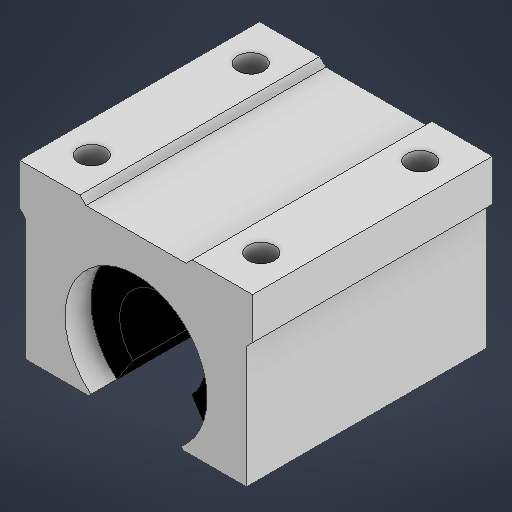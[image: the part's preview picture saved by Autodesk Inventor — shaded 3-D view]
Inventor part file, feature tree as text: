
AUTODESK INVENTOR PART (.ipt)
format: ipt  version: 2025.1 (Build 291241000, 241)  size: 246,272 bytes
history: native  units: mm
features: extrude x3, sketch x2
ambient origin geometry x8: Origin, YZ Plane, XZ Plane, XY Plane, X Axis, Y Axis, Z Axis, Center Point
bodies: Solid1 (feature_tree)
feature tree (5):
  sketch  "Sketch1"  dims[d1=44.0mm d2=32.0mm d3=135.0deg]
  extrude  "Extrusion1"  Depth=32.0mm TaperAngle=135.0deg
  extrude  "Extrusion2"  Depth=15.0mm
  extrude  "Extrusion3"  TaperAngle=45.0deg  [1 undecoded]
  sketch  "Sketch2"  dims[d4=135.0deg d5=18.9mm d6=45.0deg d7=32.0mm d8=23.0mm d9=135.0deg d10=23.0mm d11=1.15mm d12=1.15mm d13=16.0mm d14=11.0mm d15=5.0mm d16=6.0mm d17=5.0mm d18=32.0mm d19=5.4mm d20=45.3mm d21=0.0mm d22=35.5mm d23=0.0mm d24=5.0mm d25=5.0mm d26=30.0mm d27=5.0mm d28=5.0mm d29=30.0mm d30=32.0mm d31=15.0mm d32=0.0mm]
note: 1 required parameter value undecoded (feature->parameter linkage not recoverable at this tier; creation-order binding heuristic only, values carry confidence <= 0.55)
